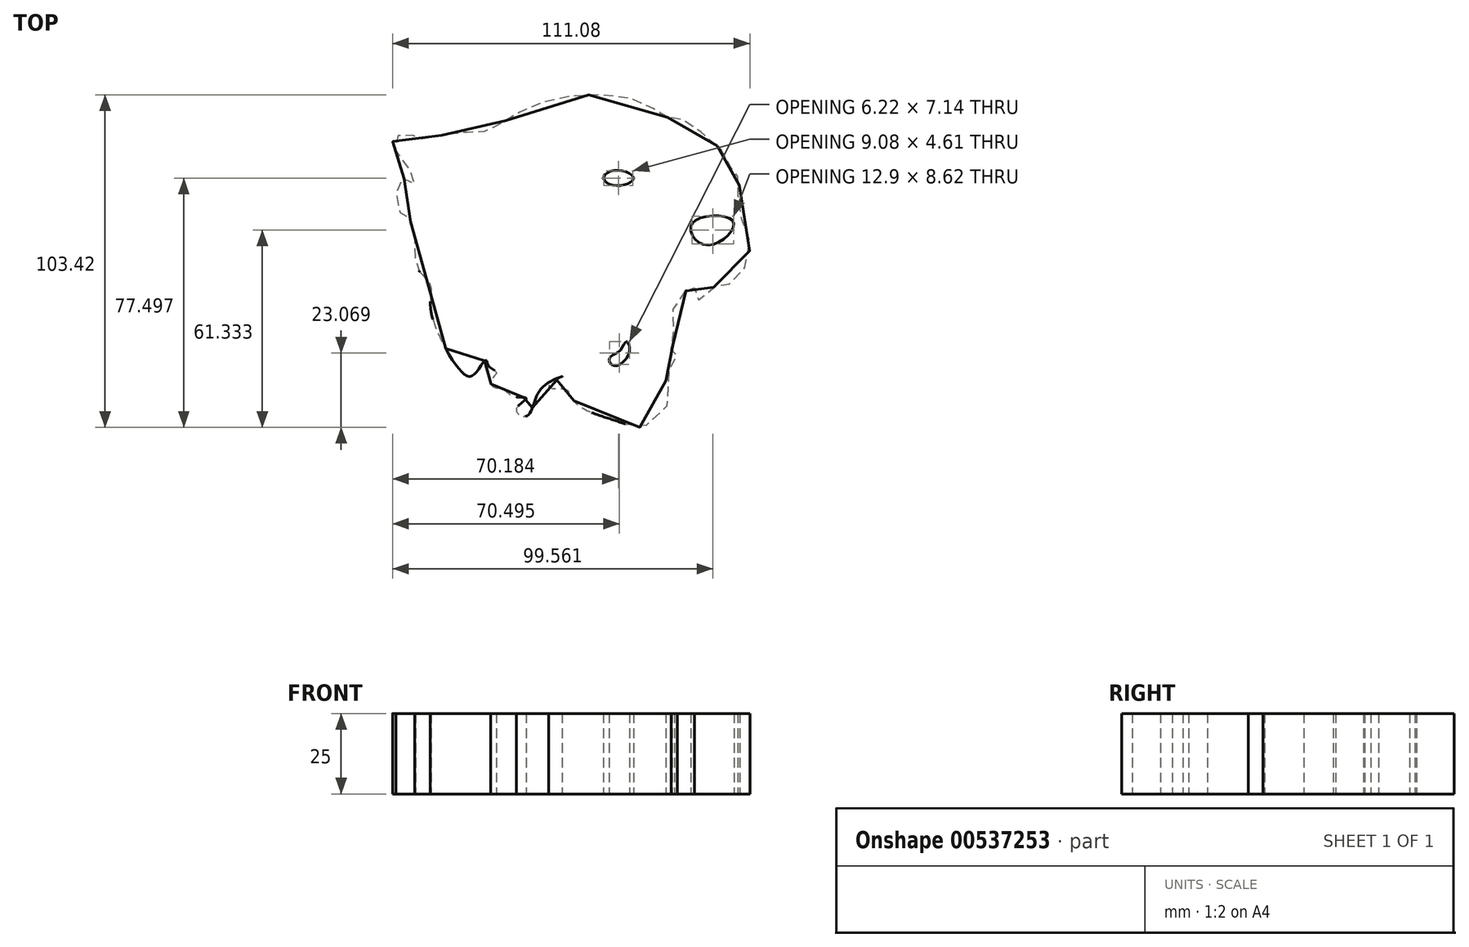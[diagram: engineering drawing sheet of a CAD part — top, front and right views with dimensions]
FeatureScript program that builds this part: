
annotation { "Feature Type Name" : "Feature", "Feature Type Description" : "" }
export const myFeature = defineFeature(function(context is Context, id is Id, definition is map)
    precondition{}
    {
        {
            var Q0;
            Q0=qCreatedBy(makeId("Top.planeOp"),FACE);
            var sketch = newSketch(context, id + "F0", { "sketchPlane" : qUnion([Q0])});
            skFitSpline(sketch, "E0", {"points": [v(28.27, 39.69) * mm, v(19.3, 44.73) * mm, v(-4.23, 45.85) * mm, v(-19.64, 40.25) * mm, v(-28.9, 35.2) * mm, v(-37.86, 34.93) * mm, v(-49.9, 32.96) * mm, v(-51.59, 34.37) * mm, v(-57.2, 32.4) * mm, v(-50.47, 20.92) * mm, v(-50.75, 18.95) * mm, v(-54.95, 20.64) * mm, v(-55.23, 10.27) * mm, v(-53.27, 9.7) * mm, v(-50.19, 0) * mm, v(-49.9, -6.82) * mm, v(-45.7, -12.15) * mm, v(-45.42, -20) * mm, v(-37.3, -37.65) * mm, v(-32.53, -40.73) * mm, v(-28.9, -36.24) * mm, v(-28.05, -35.96) * mm, v(-27.5, -37.65) * mm, v(-24.97, -39.6) * mm, v(-26.37, -41.57) * mm, v(-26.37, -43.8) * mm, v(-23, -44.93) * mm, v(-21.33, -46.05) * mm, v(-19.36, -47.17) * mm, v(-15.72, -47.73) * mm, v(-18.8, -51.1) * mm, v(-16, -53.34) * mm, v(-13.48, -49.7) * mm, v(-9.56, -43.25) * mm, v(-4.51, -41) * mm, v(-8.72, -43.8) * mm, v(-7.04, -44.65) * mm, v(-3.4, -44.93) * mm, v(0, -49.41) * mm, v(13.14, -55.02) * mm, v(21.54, -56.14) * mm, v(29.39, -46.61) * mm, v(27.7, -42.69) * mm, v(30.8, -35.4) * mm, v(31.07, -34.28) * mm, v(29.39, -33.72) * mm, v(30.23, -29.8) * mm, v(29.67, -21.4) * mm, v(33.31, -14.95) * mm, v(36.4, -12.43) * mm, v(36.96, -17.2) * mm, v(42.84, -12.99) * mm, v(45.64, -12.7) * mm, v(51.25, -8.79) * mm, v(53.49, 2.98) * mm, v(50.12, 11.67) * mm, v(50.4, 20.92) * mm, v(48.44, 22.32) * mm, v(47.32, 26.24) * mm, v(39.48, 34.37) * mm, v(32.47, 39.13) * mm, v(28.27, 39.69) * mm]});
            skFitSpline(sketch, "E1", {"points": [v(10.12, -35.2) * mm, v(13.18, -33.07) * mm, v(15.53, -30) * mm, v(16.24, -33.54) * mm, v(11.54, -37.55) * mm, v(10.12, -35.2) * mm]});
            skFitSpline(sketch, "E2", {"points": [v(8.38, 21.3) * mm, v(10.03, 18.96) * mm, v(16.16, 19.2) * mm, v(17.57, 21.09) * mm, v(12.85, 23.2) * mm, v(8.38, 21.3) * mm]});
            skFitSpline(sketch, "E3", {"points": [v(35.95, 6.76) * mm, v(40.44, 0) * mm, v(48.67, 7.25) * mm, v(35.95, 6.76) * mm]});
            skSolve(sketch);
        }
        {
            var Q0;
            Q0=makeQuery(id+"F0.imprint","IMPRINT",FACE,{"disambiguationData":[TD([[makeQuery(id+"F0.imprint","IMPRINT",EDGE,{"derivedFrom":sQuery(id+"F0.wireOp",EDGE,"E0")}),1.0]])]});
            extrude(context, id + "F1", {"entities" : qUnion([Q0]), "depth" : 25 * mm, "offsetDistance" : 25 * mm});
        }
    });
